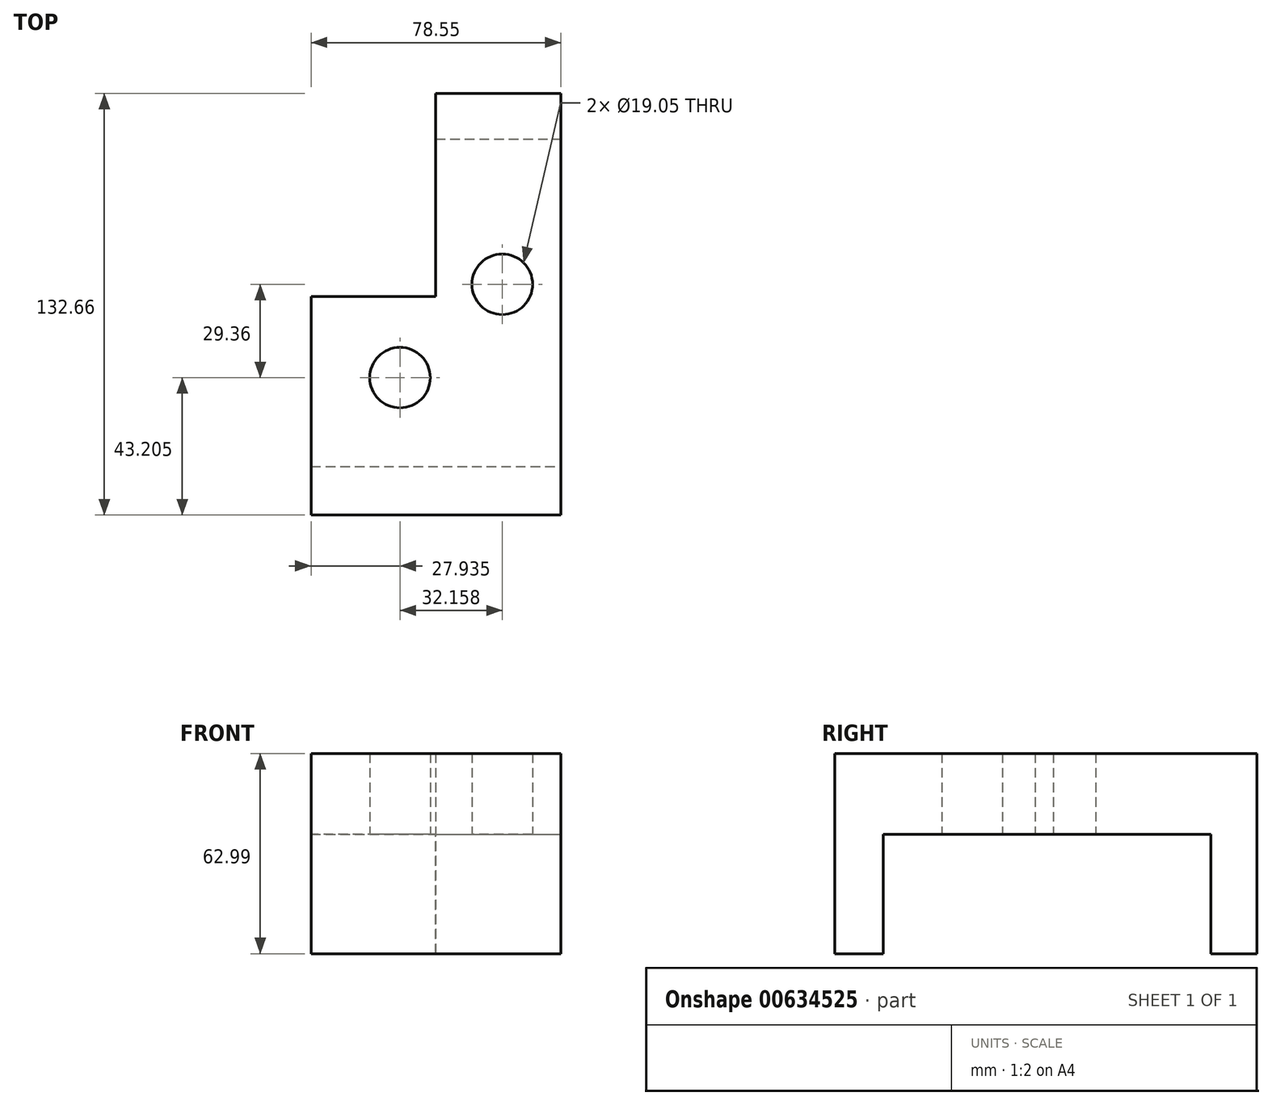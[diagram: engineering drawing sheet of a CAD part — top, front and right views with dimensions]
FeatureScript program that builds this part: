
annotation { "Feature Type Name" : "Feature", "Feature Type Description" : "" }
export const myFeature = defineFeature(function(context is Context, id is Id, definition is map)
    precondition{}
    {
        {
            var Q0;
            Q0=qCreatedBy(makeId("Top.planeOp"),FACE);
            var sketch = newSketch(context, id + "F0", { "sketchPlane" : qUnion([Q0])});
            skLineSegment(sketch, "E0", {"start": v(-24.06, 63.96) * mm, "end": v(-24.06, 0) * mm});
            skLineSegment(sketch, "E1", {"start": v(-24.06, 0) * mm, "end": v(-63.21, 0) * mm});
            skLineSegment(sketch, "E2", {"start": v(-63.21, 0) * mm, "end": v(-63.21, -68.7) * mm});
            skLineSegment(sketch, "E3", {"start": v(-63.21, -68.7) * mm, "end": v(15.34, -68.7) * mm});
            skLineSegment(sketch, "E4", {"start": v(15.34, -68.7) * mm, "end": v(15.34, 63.96) * mm});
            skLineSegment(sketch, "E5", {"start": v(15.34, 63.96) * mm, "end": v(-24.06, 63.96) * mm});
            skLineSegment(sketch, "E6", {"start": v(-63.21, -53.49) * mm, "end": v(15.34, -53.49) * mm});
            skLineSegment(sketch, "E7", {"start": v(-24.06, 49.5) * mm, "end": v(15.34, 49.5) * mm});
            skCircle(sketch, "E8", {"center": v(-3.12, 3.87) * mm, "radius": 9.53 * mm});
            skCircle(sketch, "E9", {"center": v(-35.27, -25.5) * mm, "radius": 9.53 * mm});
            skSolve(sketch);
        }
        {
            var Q0;
            Q0 = qSketchRegion(id + "F0", true);
            extrude(context, id + "F1", {"entities" : qUnion([Q0]), "depth" : 25.4 * mm, "offsetDistance" : 25.4 * mm});
        }
        {
            var Q0;
            {var subQ0=sQuery(id+"F0.wireOp",EDGE,"E5");Q0=makeQuery(id+"F0.imprint","IMPRINT",FACE,{"disambiguationData":[TD([[makeQuery(id+"F0.imprint","IMPRINT",EDGE,{"derivedFrom":subQ0}),1.0]])]});}
            var Q1;
            {var subQ0=sQuery(id+"F0.wireOp",EDGE,"E3");Q1=makeQuery(id+"F0.imprint","IMPRINT",FACE,{"disambiguationData":[TD([[makeQuery(id+"F0.imprint","IMPRINT",EDGE,{"derivedFrom":subQ0}),1.0]])]});}
            extrude(context, id + "F2", {"entities" : qUnion([Q0, Q1]), "operationType" : NewBodyOperationType.ADD, "oppositeDirection" : true, "depth" : 37.6 * mm, "offsetDistance" : 25.4 * mm});
        }
    });
